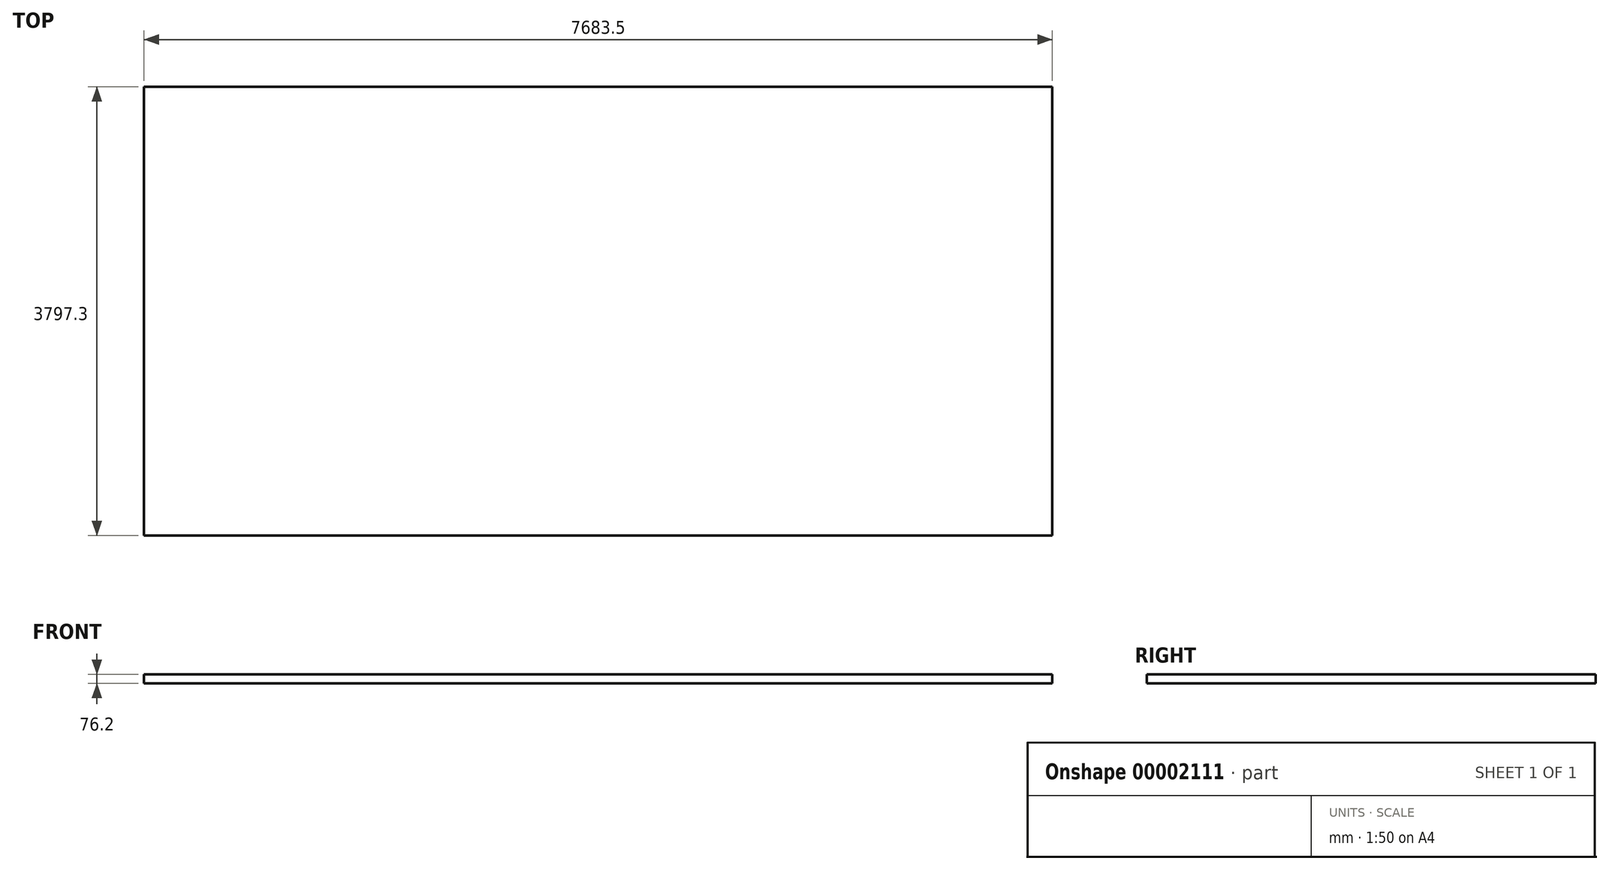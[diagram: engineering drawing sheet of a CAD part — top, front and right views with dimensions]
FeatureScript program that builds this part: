
annotation { "Feature Type Name" : "Feature", "Feature Type Description" : "" }
export const myFeature = defineFeature(function(context is Context, id is Id, definition is map)
    precondition{}
    {
        {
            var Q0;
            Q0=qCreatedBy(makeId("Top.planeOp"),FACE);
            var sketch = newSketch(context, id + "F0", { "sketchPlane" : qUnion([Q0])});
            skLineSegment(sketch, "E0.bottom", {"start": v(-60.81, 3674.91) * mm, "end": v(7622.69, 3674.91) * mm});
            skLineSegment(sketch, "E0.top", {"start": v(-60.81, -122.39) * mm, "end": v(7622.69, -122.39) * mm});
            skLineSegment(sketch, "E0.left", {"start": v(-60.81, 3674.91) * mm, "end": v(-60.81, -122.39) * mm});
            skLineSegment(sketch, "E0.right", {"start": v(7622.69, 3674.91) * mm, "end": v(7622.69, -122.39) * mm});
            skSolve(sketch);
        }
        {
            var Q0;
            Q0=makeQuery(id+"F0.imprint","IMPRINT",FACE,{"disambiguationData":[TD([[makeQuery(id+"F0.imprint","IMPRINT",EDGE,{"derivedFrom":sQuery(id+"F0.wireOp",EDGE,"E0.bottom")}),-1.0]])]});
            extrude(context, id + "F1", {"entities" : qUnion([Q0]), "oppositeDirection" : true, "depth" : 76.2 * mm});
        }
    });
